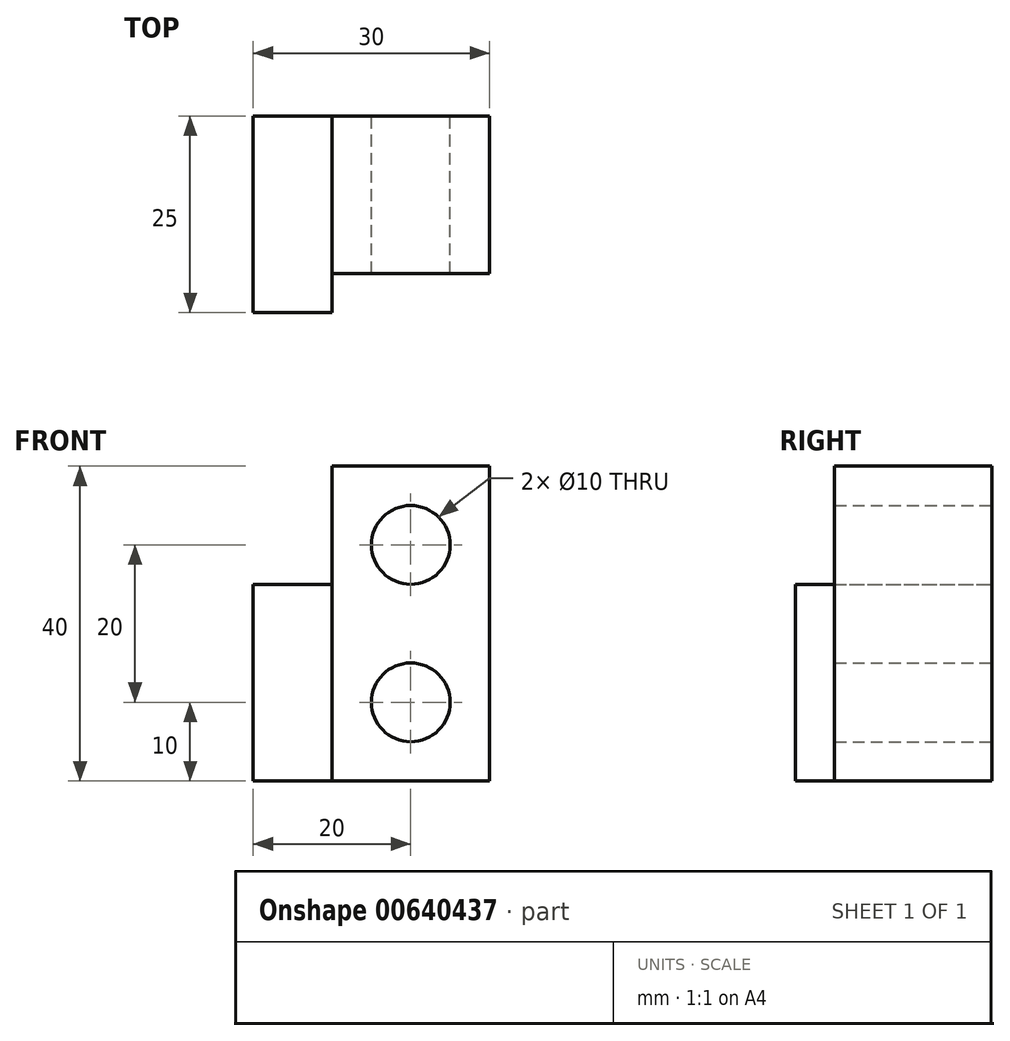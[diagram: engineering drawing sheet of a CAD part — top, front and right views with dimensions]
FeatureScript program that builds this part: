
annotation { "Feature Type Name" : "Feature", "Feature Type Description" : "" }
export const myFeature = defineFeature(function(context is Context, id is Id, definition is map)
    precondition{}
    {
        {
            var Q0;
            Q0=qCreatedBy(makeId("Front.planeOp"),FACE);
            var sketch = newSketch(context, id + "F0", { "sketchPlane" : qUnion([Q0])});
            skLineSegment(sketch, "E0.bottom", {"start": v(10, 20) * mm, "end": v(-10, 20) * mm});
            skLineSegment(sketch, "E0.top", {"start": v(10, -20) * mm, "end": v(-10, -20) * mm});
            skLineSegment(sketch, "E0.left", {"start": v(10, 20) * mm, "end": v(10, -20) * mm});
            skLineSegment(sketch, "E0.right", {"start": v(-10, 20) * mm, "end": v(-10, -20) * mm});
            skPoint(sketch, "E0.middle", {"position": v(0, 0) * mm});
            skLineSegment(sketch, "E1.bottom", {"start": v(-10, -20) * mm, "end": v(-20, -20) * mm});
            skLineSegment(sketch, "E1.top", {"start": v(-10, 5) * mm, "end": v(-20, 5) * mm});
            skLineSegment(sketch, "E1.left", {"start": v(-10, -20) * mm, "end": v(-10, 5) * mm});
            skLineSegment(sketch, "E1.right", {"start": v(-20, -20) * mm, "end": v(-20, 5) * mm});
            skCircle(sketch, "E2", {"center": v(0, -10) * mm, "radius": 5 * mm});
            skSolve(sketch);
        }
        {
            var Q0;
            Q0=makeQuery(id+"F0.imprint","IMPRINT",FACE,{"disambiguationData":[TD([[makeQuery(id+"F0.imprint","IMPRINT",EDGE,{"derivedFrom":sQuery(id+"F0.wireOp",EDGE,"E1.bottom")}),-1.0]])]});
            extrude(context, id + "F1", {"entities" : qUnion([Q0]), "depth" : 5 * mm, "offsetDistance" : 25 * mm});
        }
        {
            var Q0;
            Q0 = qSketchRegion(id + "F0", true);
            var Q1;
            Q1=makeQuery(id+"F1.opExtrude","CAP_FACE",FACE,{"disambiguationData":[OSD([sQuery(id+"F0.wireOp",EDGE,"E1.bottom"),sQuery(id+"F0.wireOp",EDGE,"E1.top"),sQuery(id+"F0.wireOp",EDGE,"E1.left"),sQuery(id+"F0.wireOp",EDGE,"E1.right")])],"isStart":false});
            extrude(context, id + "F2", {"entities" : qUnion([Q0, Q1]), "operationType" : NewBodyOperationType.ADD, "depth" : 20 * mm, "offsetDistance" : 25 * mm});
        }
        {
            var Q0;
            Q0=qCreatedBy(makeId("Front.planeOp"),FACE);
            var sketch = newSketch(context, id + "F3", { "sketchPlane" : qUnion([Q0])});
            skCircle(sketch, "E3", {"center": v(0, 10) * mm, "radius": 5 * mm});
            skPoint(sketch, "E3.centerSnap0", {"position": v(-10, 12.5) * mm});
            skSolve(sketch);
        }
        {
            var Q0;
            Q0=makeQuery(id+"F3.imprint","IMPRINT",FACE,{"disambiguationData":[TD([[makeQuery(id+"F3.imprint","IMPRINT",EDGE,{"derivedFrom":sQuery(id+"F3.wireOp",EDGE,"E3")}),1.0]])]});
            var Q1;
            Q1=sQuery(id+"F3.wireOp",EDGE,"E3");
            extrude(context, id + "F4", {"entities" : qUnion([Q0]), "operationType" : NewBodyOperationType.REMOVE, "surfaceEntities" : qUnion([Q1]), "depth" : 68.9 * mm, "offsetDistance" : 25 * mm});
        }
    });
